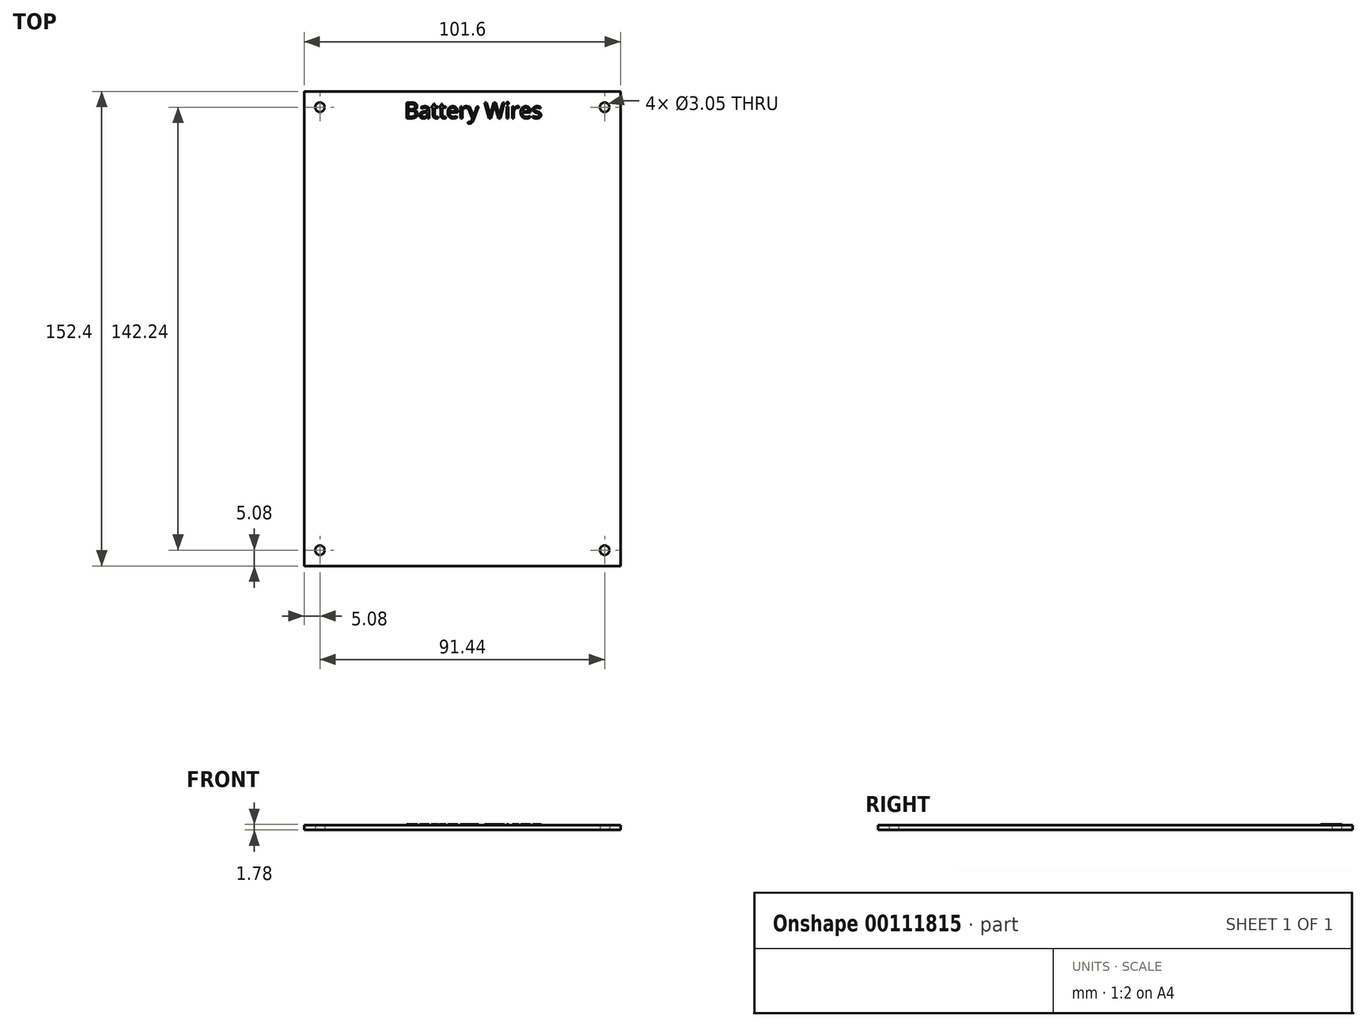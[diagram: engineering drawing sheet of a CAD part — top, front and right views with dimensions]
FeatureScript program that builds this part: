
annotation { "Feature Type Name" : "Feature", "Feature Type Description" : "" }
export const myFeature = defineFeature(function(context is Context, id is Id, definition is map)
    precondition{}
    {
        {
            var Q0;
            Q0=qCreatedBy(makeId("Top.planeOp"),FACE);
            var sketch = newSketch(context, id + "F0", { "sketchPlane" : qUnion([Q0])});
            skLineSegment(sketch, "E0.bottom", {"start": v(50.8, -76.2) * mm, "end": v(-50.8, -76.2) * mm});
            skLineSegment(sketch, "E0.top", {"start": v(50.8, 76.2) * mm, "end": v(-50.8, 76.2) * mm});
            skLineSegment(sketch, "E0.left", {"start": v(50.8, -76.2) * mm, "end": v(50.8, 76.2) * mm});
            skLineSegment(sketch, "E0.right", {"start": v(-50.8, -76.2) * mm, "end": v(-50.8, 76.2) * mm});
            skPoint(sketch, "E0.middle", {"position": v(0, 0) * mm});
            skCircle(sketch, "E1", {"center": v(-45.72, 71.12) * mm, "radius": 1.52 * mm});
            skCircle(sketch, "E2.0.1.0", {"center": v(-45.72, -71.12) * mm, "radius": 1.52 * mm});
            skCircle(sketch, "E2.1.0.0", {"center": v(45.72, 71.12) * mm, "radius": 1.52 * mm});
            skCircle(sketch, "E2.1.1.0", {"center": v(45.72, -71.12) * mm, "radius": 1.52 * mm});
            skLineSegment(sketch, "E2.direction1", {"start": v(-45.72, 71.12) * mm, "end": v(45.72, 71.12) * mm, "construction": true});
            skLineSegment(sketch, "E2.direction2", {"start": v(-45.72, 71.12) * mm, "end": v(-45.72, -71.12) * mm, "construction": true});
            skSolve(sketch);
        }
        {
            var Q0;
            Q0=makeQuery(id+"F0.imprint","IMPRINT",FACE,{"disambiguationData":[TD([[makeQuery(id+"F0.imprint","IMPRINT",EDGE,{"derivedFrom":sQuery(id+"F0.wireOp",EDGE,"E0.bottom")}),-1.0]])]});
            extrude(context, id + "F1", {"entities" : qUnion([Q0]), "depth" : 1.52 * mm});
        }
        {
            var Q0;
            Q0=makeQuery(id+"F1.opExtrude","CAP_FACE",FACE,{"disambiguationData":[OSD([sQuery(id+"F0.wireOp",EDGE,"E0.bottom"),sQuery(id+"F0.wireOp",EDGE,"E0.top"),sQuery(id+"F0.wireOp",EDGE,"E0.left"),sQuery(id+"F0.wireOp",EDGE,"E0.right"),sQuery(id+"F0.wireOp",EDGE,"E1"),sQuery(id+"F0.wireOp",EDGE,"E2.0.1.0"),sQuery(id+"F0.wireOp",EDGE,"E2.1.0.0"),sQuery(id+"F0.wireOp",EDGE,"E2.1.1.0")])],"isStart":false});
            var sketch = newSketch(context, id + "F2", { "sketchPlane" : qUnion([Q0])});
            skText(sketch, "E3", { "text": "Battery Wires\n", "fontName": "OpenSans-Regular.ttf"});
            const initialGuessF2  = {"E3": [-0.01857, 0.0676, 1, 0, 0.00508]};
            skSetInitialGuess(sketch, initialGuessF2);
            skSolve(sketch);
        }
        {
            var Q0;
            Q0 = qSketchRegion(id + "F2", true);
            extrude(context, id + "F3", {"entities" : qUnion([Q0]), "operationType" : NewBodyOperationType.ADD, "depth" : 0.25 * mm});
        }
    });
